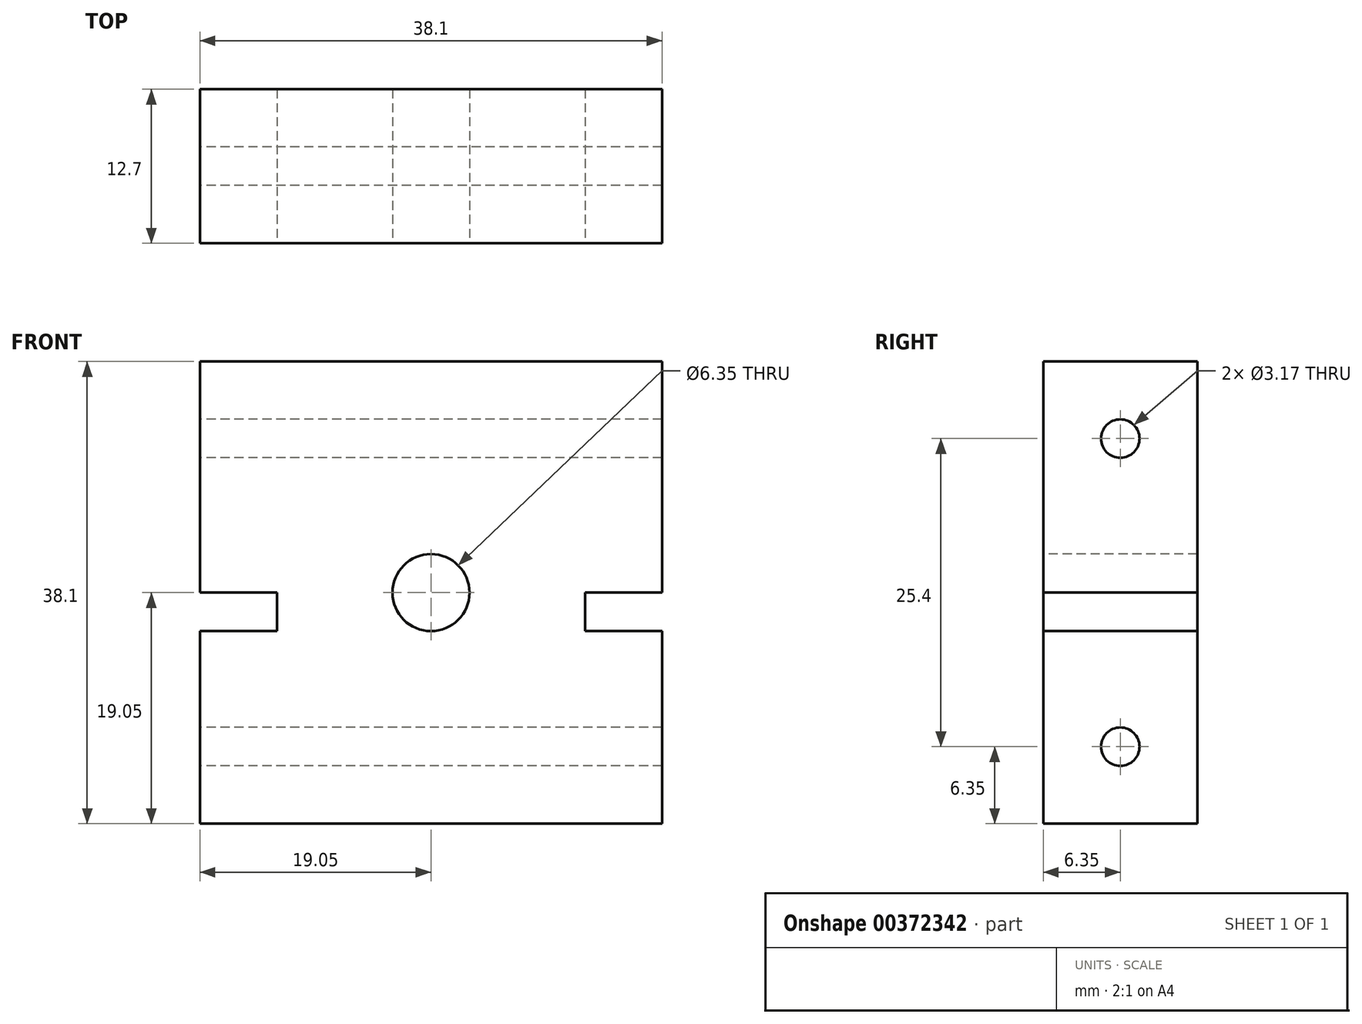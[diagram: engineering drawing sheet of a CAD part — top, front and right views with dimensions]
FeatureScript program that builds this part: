
annotation { "Feature Type Name" : "Feature", "Feature Type Description" : "" }
export const myFeature = defineFeature(function(context is Context, id is Id, definition is map)
    precondition{}
    {
        {
            var Q0;
            Q0=qCreatedBy(makeId("Front.planeOp"),FACE);
            var sketch = newSketch(context, id + "F0", { "sketchPlane" : qUnion([Q0])});
            skLineSegment(sketch, "E0.bottom", {"start": v(-19.05, 19.05) * mm, "end": v(19.05, 19.05) * mm});
            skLineSegment(sketch, "E0.top", {"start": v(-19.05, -19.05) * mm, "end": v(19.05, -19.05) * mm});
            skLineSegment(sketch, "E0.left", {"start": v(-19.05, 19.05) * mm, "end": v(-19.05, -19.05) * mm});
            skLineSegment(sketch, "E0.right", {"start": v(19.05, 19.05) * mm, "end": v(19.05, -19.05) * mm});
            skSolve(sketch);
        }
        {
            var Q0;
            Q0=qCreatedBy(makeId("Front.planeOp"),FACE);
            var sketch = newSketch(context, id + "F1", { "sketchPlane" : qUnion([Q0])});
            skCircle(sketch, "E1", {"center": v(0, 0) * mm, "radius": 3.18 * mm});
            skSolve(sketch);
        }
        {
            var Q0;
            Q0=qCreatedBy(makeId("Front.planeOp"),FACE);
            var sketch = newSketch(context, id + "F2", { "sketchPlane" : qUnion([Q0])});
            skLineSegment(sketch, "E2.bottom", {"start": v(-19.05, 0) * mm, "end": v(-12.7, 0) * mm});
            skLineSegment(sketch, "E2.top", {"start": v(-19.05, -3.18) * mm, "end": v(-12.7, -3.18) * mm});
            skLineSegment(sketch, "E2.left", {"start": v(-19.05, 0) * mm, "end": v(-19.05, -3.18) * mm});
            skLineSegment(sketch, "E2.right", {"start": v(-12.7, 0) * mm, "end": v(-12.7, -3.18) * mm});
            skSolve(sketch);
        }
        {
            var Q0;
            Q0=qCreatedBy(makeId("Front.planeOp"),FACE);
            var sketch = newSketch(context, id + "F3", { "sketchPlane" : qUnion([Q0])});
            skLineSegment(sketch, "E3.bottom", {"start": v(12.7, 0) * mm, "end": v(19.05, 0) * mm});
            skLineSegment(sketch, "E3.top", {"start": v(12.7, -3.17) * mm, "end": v(19.05, -3.17) * mm});
            skLineSegment(sketch, "E3.left", {"start": v(12.7, 0) * mm, "end": v(12.7, -3.17) * mm});
            skLineSegment(sketch, "E3.right", {"start": v(19.05, 0) * mm, "end": v(19.05, -3.17) * mm});
            skSolve(sketch);
        }
        {
            var Q0;
            Q0=qCreatedBy(makeId("Right.planeOp"),FACE);
            var sketch = newSketch(context, id + "F4", { "sketchPlane" : qUnion([Q0])});
            skCircle(sketch, "E4", {"center": v(0, 12.7) * mm, "radius": 1.59 * mm});
            skSolve(sketch);
        }
        {
            var Q0;
            Q0=qCreatedBy(makeId("Right.planeOp"),FACE);
            var sketch = newSketch(context, id + "F5", { "sketchPlane" : qUnion([Q0])});
            skCircle(sketch, "E5", {"center": v(0, -12.7) * mm, "radius": 1.59 * mm});
            skSolve(sketch);
        }
        {
            var Q0;
            Q0 = qSketchRegion(id + "F0", true);
            extrude(context, id + "F6", {"entities" : qUnion([Q0]), "endBound" : BoundingType.SYMMETRIC, "depth" : 12.7 * mm});
        }
        {
            var Q0;
            Q0 = qSketchRegion(id + "F1", true);
            extrude(context, id + "F7", {"entities" : qUnion([Q0]), "operationType" : NewBodyOperationType.REMOVE, "endBound" : BoundingType.SYMMETRIC, "oppositeDirection" : true, "depth" : 12.7 * mm});
        }
        {
            var Q0;
            Q0 = qSketchRegion(id + "F2", true);
            var Q1;
            Q1 = qSketchRegion(id + "F3", true);
            extrude(context, id + "F8", {"entities" : qUnion([Q0, Q1]), "operationType" : NewBodyOperationType.REMOVE, "endBound" : BoundingType.SYMMETRIC, "oppositeDirection" : true, "depth" : 12.7 * mm});
        }
        {
            var Q0;
            Q0 = qSketchRegion(id + "F4", true);
            var Q1;
            Q1 = qSketchRegion(id + "F5", true);
            extrude(context, id + "F9", {"entities" : qUnion([Q0, Q1]), "operationType" : NewBodyOperationType.REMOVE, "endBound" : BoundingType.SYMMETRIC, "depth" : 38.1 * mm});
        }
    });
